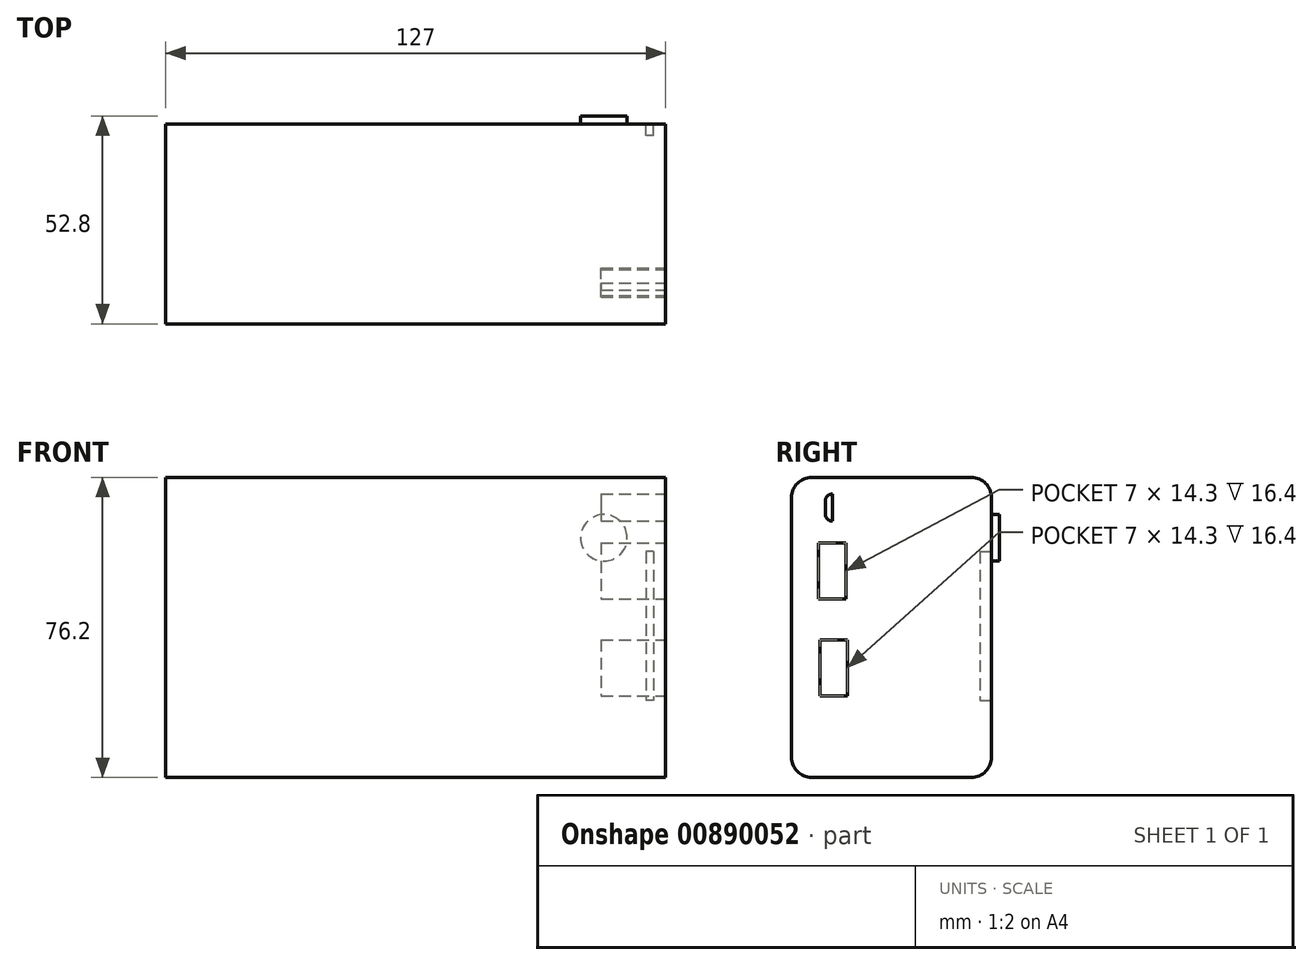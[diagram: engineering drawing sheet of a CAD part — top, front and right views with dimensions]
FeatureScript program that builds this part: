
annotation { "Feature Type Name" : "Feature", "Feature Type Description" : "" }
export const myFeature = defineFeature(function(context is Context, id is Id, definition is map)
    precondition{}
    {
        {
            var Q0;
            Q0=qCreatedBy(makeId("Front.planeOp"),FACE);
            var sketch = newSketch(context, id + "F0", { "sketchPlane" : qUnion([Q0])});
            skLineSegment(sketch, "E0.bottom", {"start": v(63.5, -38.1) * mm, "end": v(-63.5, -38.1) * mm});
            skLineSegment(sketch, "E0.top", {"start": v(63.5, 38.1) * mm, "end": v(-63.5, 38.1) * mm});
            skLineSegment(sketch, "E0.left", {"start": v(63.5, -38.1) * mm, "end": v(63.5, 38.1) * mm});
            skLineSegment(sketch, "E0.right", {"start": v(-63.5, -38.1) * mm, "end": v(-63.5, 38.1) * mm});
            skPoint(sketch, "E0.middle", {"position": v(0, 0) * mm});
            skSolve(sketch);
        }
        {
            var Q0;
            Q0 = qSketchRegion(id + "F0", true);
            extrude(context, id + "F1", {"entities" : qUnion([Q0]), "oppositeDirection" : true, "depth" : 50.8 * mm, "offsetDistance" : 25.4 * mm});
        }
        {
            var Q0;
            Q0=makeQuery(id+"F1.opExtrude","CAP_EDGE",EDGE,{"disambiguationData":[OSD([sQuery(id+"F0.wireOp",EDGE,"E0.bottom")])],"isStart":false});
            var Q1;
            Q1=makeQuery(id+"F1.opExtrude","CAP_EDGE",EDGE,{"disambiguationData":[OSD([sQuery(id+"F0.wireOp",EDGE,"E0.bottom")])],"isStart":true});
            var Q2;
            Q2=makeQuery(id+"F1.opExtrude","CAP_EDGE",EDGE,{"disambiguationData":[OSD([sQuery(id+"F0.wireOp",EDGE,"E0.top")])],"isStart":true});
            var Q3;
            Q3=makeQuery(id+"F1.opExtrude","CAP_EDGE",EDGE,{"disambiguationData":[OSD([sQuery(id+"F0.wireOp",EDGE,"E0.top")])],"isStart":false});
            fillet(context, id + "F2", {"entities" : qUnion([Q0, Q1, Q2, Q3]), "radius" : 5.08 * mm, "tangentPropagation" : true, "allowEdgeOverflow" : false});
        }
        {
            var Q0;
            Q0=makeQuery(id+"F1.opExtrude","SWEPT_FACE",FACE,{"disambiguationData":[OSD([sQuery(id+"F0.wireOp",EDGE,"E0.left")])]});
            var sketch = newSketch(context, id + "F3", { "sketchPlane" : qUnion([Q0])});
            skLineSegment(sketch, "E1.bottom", {"start": v(6.83, 21.47) * mm, "end": v(13.83, 21.47) * mm});
            skLineSegment(sketch, "E1.top", {"start": v(6.83, 7.17) * mm, "end": v(13.83, 7.17) * mm});
            skLineSegment(sketch, "E1.left", {"start": v(6.83, 21.47) * mm, "end": v(6.83, 7.17) * mm});
            skLineSegment(sketch, "E1.right", {"start": v(13.83, 21.47) * mm, "end": v(13.83, 7.17) * mm});
            skSolve(sketch);
        }
        {
            var Q0;
            Q0=makeQuery(id+"F3.imprint","IMPRINT",FACE,{"disambiguationData":[TD([[makeQuery(id+"F3.imprint","IMPRINT",EDGE,{"derivedFrom":sQuery(id+"F3.wireOp",EDGE,"E1.bottom")}),-1.0]])]});
            extrude(context, id + "F4", {"entities" : qUnion([Q0]), "operationType" : NewBodyOperationType.REMOVE, "oppositeDirection" : true, "depth" : 16.4 * mm, "offsetDistance" : 25.4 * mm});
        }
        {
            var Q0;
            Q0=makeQuery(id+"F1.opExtrude","SWEPT_FACE",FACE,{"disambiguationData":[OSD([sQuery(id+"F0.wireOp",EDGE,"E0.left")])]});
            var sketch = newSketch(context, id + "F5", { "sketchPlane" : qUnion([Q0])});
            skLineSegment(sketch, "E2.bottom", {"start": v(7.22, -3.12) * mm, "end": v(14.22, -3.12) * mm});
            skLineSegment(sketch, "E2.top", {"start": v(7.22, -17.42) * mm, "end": v(14.22, -17.42) * mm});
            skLineSegment(sketch, "E2.left", {"start": v(7.22, -3.12) * mm, "end": v(7.22, -17.42) * mm});
            skLineSegment(sketch, "E2.right", {"start": v(14.22, -3.12) * mm, "end": v(14.22, -17.42) * mm});
            skSolve(sketch);
        }
        {
            var Q0;
            Q0=makeQuery(id+"F5.imprint","IMPRINT",FACE,{"disambiguationData":[TD([[makeQuery(id+"F5.imprint","IMPRINT",EDGE,{"derivedFrom":sQuery(id+"F5.wireOp",EDGE,"E2.bottom")}),-1.0]])]});
            extrude(context, id + "F6", {"entities" : qUnion([Q0]), "operationType" : NewBodyOperationType.REMOVE, "oppositeDirection" : true, "depth" : 16.4 * mm, "offsetDistance" : 25.4 * mm});
        }
        {
            var Q0;
            Q0=makeQuery(id+"F1.opExtrude","SWEPT_FACE",FACE,{"disambiguationData":[OSD([sQuery(id+"F0.wireOp",EDGE,"E0.left")])]});
            var sketch = newSketch(context, id + "F7", { "sketchPlane" : qUnion([Q0])});
            skLineSegment(sketch, "E3.bottom", {"start": v(10.37, 33.9) * mm, "end": v(10.42, 33.9) * mm});
            skLineSegment(sketch, "E3.top", {"start": v(10.37, 27) * mm, "end": v(10.42, 27) * mm});
            skLineSegment(sketch, "E3.left", {"start": v(8.57, 32.1) * mm, "end": v(8.57, 28.8) * mm});
            skLineSegment(sketch, "E3.right", {"start": v(10.42, 33.9) * mm, "end": v(10.42, 27) * mm});
            skPoint(sketch, "E4.visualSharp", {"position": v(8.57, 33.9) * mm});
            skArc(sketch, "E4.filletArc", {"start": v(10.37, 33.9) * mm, "mid": v(9.1, 33.37) * mm, "end": v(8.57, 32.1) * mm});
            skPoint(sketch, "E5.visualSharp", {"position": v(8.57, 27) * mm});
            skArc(sketch, "E5.filletArc", {"start": v(8.57, 28.8) * mm, "mid": v(9.1, 27.53) * mm, "end": v(10.37, 27) * mm});
            skSolve(sketch);
        }
        {
            var Q0;
            Q0=makeQuery(id+"F7.imprint","IMPRINT",FACE,{"disambiguationData":[TD([[makeQuery(id+"F7.imprint","IMPRINT",EDGE,{"derivedFrom":sQuery(id+"F7.wireOp",EDGE,"E3.bottom")}),-1.0]])]});
            extrude(context, id + "F8", {"entities" : qUnion([Q0]), "operationType" : NewBodyOperationType.REMOVE, "oppositeDirection" : true, "depth" : 16.4 * mm, "offsetDistance" : 25.4 * mm});
        }
        {
            var Q0;
            Q0=makeQuery(id+"F1.opExtrude","CAP_FACE",FACE,{"disambiguationData":[OSD([sQuery(id+"F0.wireOp",EDGE,"E0.bottom"),sQuery(id+"F0.wireOp",EDGE,"E0.top"),sQuery(id+"F0.wireOp",EDGE,"E0.left"),sQuery(id+"F0.wireOp",EDGE,"E0.right")])],"isStart":false});
            var sketch = newSketch(context, id + "F9", { "sketchPlane" : qUnion([Q0])});
            skLineSegment(sketch, "E6.bottom", {"start": v(-60.4, 19.25) * mm, "end": v(-58.56, 19.25) * mm});
            skLineSegment(sketch, "E6.top", {"start": v(-60.4, -18.6) * mm, "end": v(-58.56, -18.6) * mm});
            skLineSegment(sketch, "E6.left", {"start": v(-60.4, 19.25) * mm, "end": v(-60.4, -18.6) * mm});
            skLineSegment(sketch, "E6.right", {"start": v(-58.56, 19.25) * mm, "end": v(-58.56, -18.6) * mm});
            skSolve(sketch);
        }
        {
            var Q0;
            Q0 = qSketchRegion(id + "F9", true);
            extrude(context, id + "F10", {"entities" : qUnion([Q0]), "operationType" : NewBodyOperationType.REMOVE, "oppositeDirection" : true, "depth" : 3 * mm, "offsetDistance" : 25.4 * mm});
        }
        {
            var Q0;
            Q0=makeQuery(id+"F1.opExtrude","CAP_FACE",FACE,{"disambiguationData":[OSD([sQuery(id+"F0.wireOp",EDGE,"E0.bottom"),sQuery(id+"F0.wireOp",EDGE,"E0.top"),sQuery(id+"F0.wireOp",EDGE,"E0.left"),sQuery(id+"F0.wireOp",EDGE,"E0.right")])],"isStart":false});
            var sketch = newSketch(context, id + "F11", { "sketchPlane" : qUnion([Q0])});
            skCircle(sketch, "E7", {"center": v(-47.83, 22.76) * mm, "radius": 5.92 * mm});
            skPoint(sketch, "E7.first.point", {"position": v(-53.24, 25.18) * mm});
            skPoint(sketch, "E7.second.point", {"position": v(-46.49, 17) * mm});
            skPoint(sketch, "E7.third.point", {"position": v(-44.03, 18.23) * mm});
            skSolve(sketch);
        }
        {
            var Q0;
            Q0=makeQuery(id+"F11.imprint","IMPRINT",FACE,{"disambiguationData":[TD([[makeQuery(id+"F11.imprint","IMPRINT",EDGE,{"derivedFrom":sQuery(id+"F11.wireOp",EDGE,"E7")}),1.0]])]});
            extrude(context, id + "F12", {"entities" : qUnion([Q0]), "operationType" : NewBodyOperationType.ADD, "depth" : 2 * mm, "offsetDistance" : 25.4 * mm});
        }
    });
